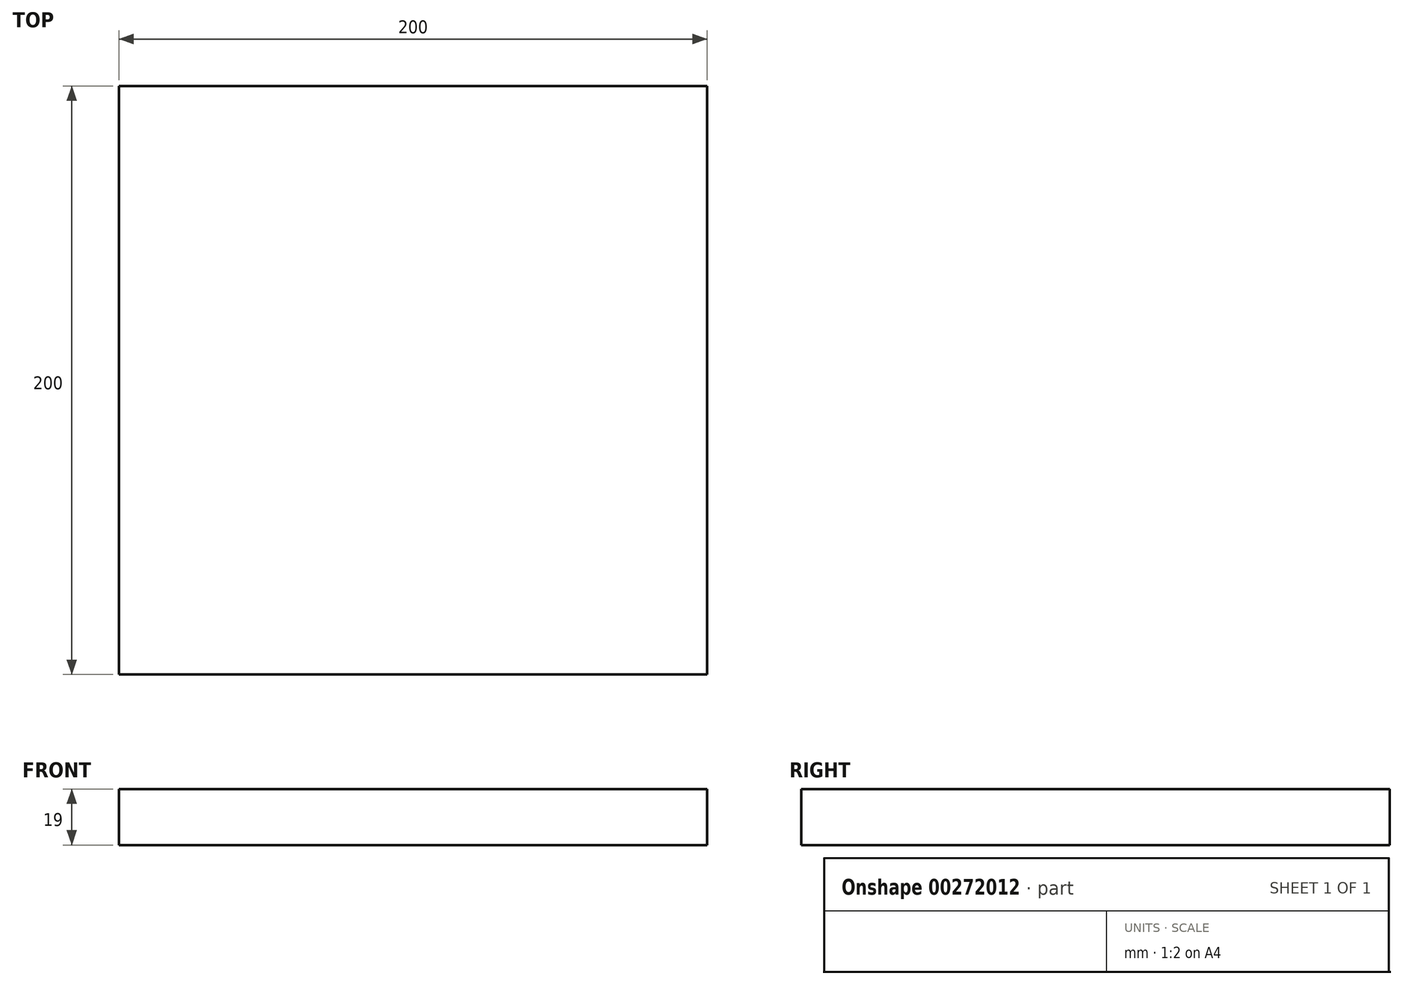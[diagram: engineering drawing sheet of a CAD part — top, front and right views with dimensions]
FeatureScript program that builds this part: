
annotation { "Feature Type Name" : "Feature", "Feature Type Description" : "" }
export const myFeature = defineFeature(function(context is Context, id is Id, definition is map)
    precondition{}
    {
        {
            var Q0;
            Q0=qCreatedBy(makeId("Front.planeOp"),FACE);
            var sketch = newSketch(context, id + "F0", { "sketchPlane" : qUnion([Q0])});
            skLineSegment(sketch, "E0.bottom", {"start": v(0, 0) * mm, "end": v(-200, 0) * mm});
            skLineSegment(sketch, "E0.top", {"start": v(0, 19) * mm, "end": v(-200, 19) * mm});
            skLineSegment(sketch, "E0.left", {"start": v(0, 0) * mm, "end": v(0, 19) * mm});
            skLineSegment(sketch, "E0.right", {"start": v(-200, 0) * mm, "end": v(-200, 19) * mm});
            skSolve(sketch);
        }
        {
            var Q0;
            Q0=makeQuery(id+"F0.imprint","IMPRINT",FACE,{"disambiguationData":[TD([[makeQuery(id+"F0.imprint","IMPRINT",EDGE,{"derivedFrom":sQuery(id+"F0.wireOp",EDGE,"E0.bottom")}),-1.0]])]});
            extrude(context, id + "F1", {"entities" : qUnion([Q0]), "oppositeDirection" : true, "depth" : 200 * mm});
        }
    });
